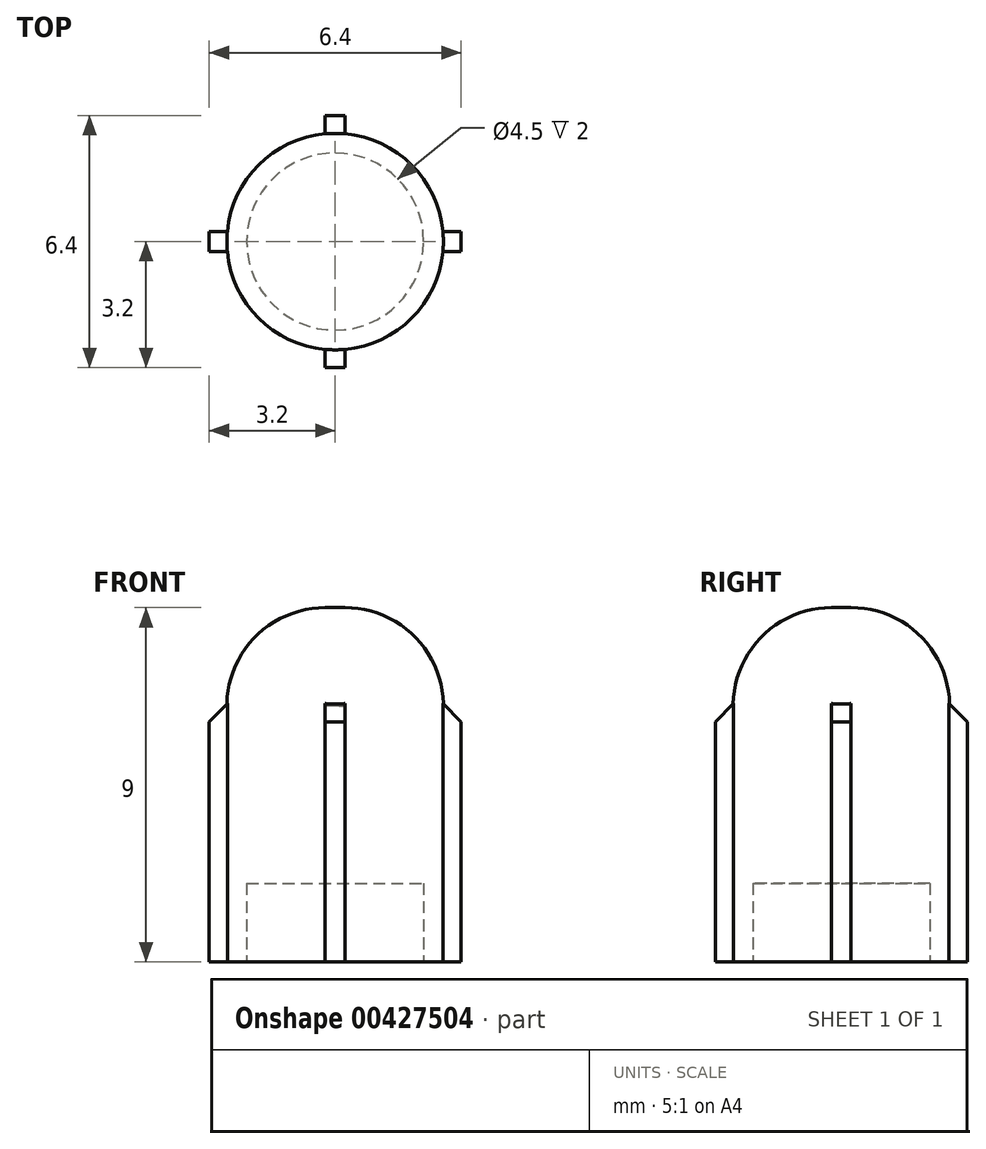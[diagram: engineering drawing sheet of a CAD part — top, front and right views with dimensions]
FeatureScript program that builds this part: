
annotation { "Feature Type Name" : "Feature", "Feature Type Description" : "" }
export const myFeature = defineFeature(function(context is Context, id is Id, definition is map)
    precondition{}
    {
        {
            var Q0;
            Q0=qCreatedBy(makeId("Top.planeOp"),FACE);
            var sketch = newSketch(context, id + "F0", { "sketchPlane" : qUnion([Q0])});
            skCircle(sketch, "E0", {"center": v(0, 0) * mm, "radius": 2.75 * mm});
            skSolve(sketch);
        }
        {
            var Q0;
            Q0 = qSketchRegion(id + "F0", true);
            extrude(context, id + "F1", {"entities" : qUnion([Q0]), "depth" : 9 * mm});
        }
        {
            var Q0;
            Q0=makeQuery(id+"F1.opExtrude","CAP_FACE",FACE,{"disambiguationData":[OSD([sQuery(id+"F0.wireOp",EDGE,"E0")])],"isStart":false});
            fillet(context, id + "F2", {"entities" : qUnion([Q0]), "radius" : 2.5 * mm, "tangentPropagation" : true, "allowEdgeOverflow" : false});
        }
        {
            var Q0;
            Q0=makeQuery(id+"F1.opExtrude","CAP_FACE",FACE,{"disambiguationData":[OSD([sQuery(id+"F0.wireOp",EDGE,"E0")])],"isStart":true});
            var sketch = newSketch(context, id + "F3", { "sketchPlane" : qUnion([Q0])});
            skLineSegment(sketch, "E1.bottom", {"start": v(-3.2, 0.25) * mm, "end": v(3.2, 0.25) * mm});
            skLineSegment(sketch, "E1.top", {"start": v(-3.2, -0.25) * mm, "end": v(3.2, -0.25) * mm});
            skLineSegment(sketch, "E1.left", {"start": v(-3.2, 0.25) * mm, "end": v(-3.2, -0.25) * mm});
            skLineSegment(sketch, "E1.right", {"start": v(3.2, 0.25) * mm, "end": v(3.2, -0.25) * mm});
            skSolve(sketch);
        }
        {
            var Q0;
            Q0 = qSketchRegion(id + "F3", true);
            extrude(context, id + "F4", {"entities" : qUnion([Q0]), "operationType" : NewBodyOperationType.ADD, "oppositeDirection" : true, "depth" : 7.5 * mm});
        }
        {
            var Q0;
            Q0=makeQuery(id+"F4.boolean.opBoolean","MERGE",FACE,{"derivedFrom":[makeQuery(id+"F1.opExtrude","CAP_FACE",FACE,{"disambiguationData":[OSD([sQuery(id+"F0.wireOp",EDGE,"E0")])],"isStart":true}),makeQuery(id+"F4.opExtrude","CAP_FACE",FACE,{"disambiguationData":[OSD([sQuery(id+"F3.wireOp",EDGE,"E1.bottom"),sQuery(id+"F3.wireOp",EDGE,"E1.top"),sQuery(id+"F3.wireOp",EDGE,"E1.left"),sQuery(id+"F3.wireOp",EDGE,"E1.right")])],"isStart":true})]});
            var sketch = newSketch(context, id + "F5", { "sketchPlane" : qUnion([Q0])});
            skLineSegment(sketch, "E2.bottom", {"start": v(-0.25, 3.2) * mm, "end": v(0.25, 3.2) * mm});
            skLineSegment(sketch, "E2.top", {"start": v(-0.25, -3.2) * mm, "end": v(0.25, -3.2) * mm});
            skLineSegment(sketch, "E2.left", {"start": v(-0.25, 3.2) * mm, "end": v(-0.25, 2.74) * mm});
            skLineSegment(sketch, "E2.right", {"start": v(0.25, 3.2) * mm, "end": v(0.25, 2.74) * mm});
            skPoint(sketch, "E3", {"position": v(0.25, 2.74) * mm});
            skPoint(sketch, "E4", {"position": v(-0.25, 2.74) * mm});
            skPoint(sketch, "E5", {"position": v(0.25, -2.74) * mm});
            skPoint(sketch, "E6", {"position": v(-0.25, -2.74) * mm});
            skLineSegment(sketch, "E7.trimOffspring", {"start": v(0.25, -2.74) * mm, "end": v(0.25, -3.2) * mm});
            skLineSegment(sketch, "E8.trimOffspring", {"start": v(-0.25, -2.74) * mm, "end": v(-0.25, -3.2) * mm});
            skFitSpline(sketch, "E9", {"points": [v(-0.25, 2.74) * mm, v(-0.11, 2.75) * mm, v(0.1, 2.75) * mm, v(0.25, 2.74) * mm], "startDerivative": vector(0.45, 0.03) * mm, "endDerivative": vector(0.47, -0.03) * mm});
            skSolve(sketch);
        }
        {
            var Q0;
            Q0=makeQuery(id+"F4.opExtrude","CAP_EDGE",EDGE,{"disambiguationData":[OSD([sQuery(id+"F3.wireOp",EDGE,"E1.left")])],"isStart":false});
            var Q1;
            Q1=makeQuery(id+"F4.opExtrude","CAP_EDGE",EDGE,{"disambiguationData":[OSD([sQuery(id+"F3.wireOp",EDGE,"E1.right")])],"isStart":false});
            chamfer(context, id + "F6", {"entities" : qUnion([Q0, Q1]), "width" : 1.4 * mm, "tangentPropagation" : true});
        }
        {
            var Q0;
            Q0=makeQuery(id+"F5.imprint","IMPRINT",FACE,{"disambiguationData":[TD([[makeQuery(id+"F5.imprint","IMPRINT",EDGE,{"derivedFrom":sQuery(id+"F5.wireOp",EDGE,"E2.bottom")}),-1.0]])]});
            var Q1;
            Q1=makeQuery(id+"F5.imprint","IMPRINT",FACE,{"disambiguationData":[TD([[makeQuery(id+"F5.imprint","IMPRINT",EDGE,{"derivedFrom":sQuery(id+"F5.wireOp",EDGE,"E2.top")}),1.0]])]});
            extrude(context, id + "F7", {"entities" : qUnion([Q0, Q1]), "operationType" : NewBodyOperationType.ADD, "oppositeDirection" : true, "depth" : 7.5 * mm});
        }
        {
            var Q0;
            Q0=makeQuery(id+"F7.opExtrude","CAP_EDGE",EDGE,{"disambiguationData":[OSD([sQuery(id+"F5.wireOp",EDGE,"E2.top")])],"isStart":false});
            var Q1;
            Q1=makeQuery(id+"F7.opExtrude","CAP_EDGE",EDGE,{"disambiguationData":[OSD([sQuery(id+"F5.wireOp",EDGE,"E2.bottom")])],"isStart":false});
            chamfer(context, id + "F8", {"entities" : qUnion([Q0, Q1]), "width" : 1.4 * mm, "tangentPropagation" : true});
        }
        {
            var Q0;
            {var subQ0=sQuery(id+"F0.wireOp",EDGE,"E0");Q0=makeQuery(id+"F7.boolean.opBoolean","MERGE",FACE,{"derivedFrom":[makeQuery(id+"F4.boolean.opBoolean","MERGE",FACE,{"derivedFrom":[makeQuery(id+"F1.opExtrude","CAP_FACE",FACE,{"disambiguationData":[OSD([subQ0])],"isStart":true}),makeQuery(id+"F4.opExtrude","CAP_FACE",FACE,{"disambiguationData":[OSD([sQuery(id+"F3.wireOp",EDGE,"E1.bottom"),sQuery(id+"F3.wireOp",EDGE,"E1.top"),sQuery(id+"F3.wireOp",EDGE,"E1.left"),sQuery(id+"F3.wireOp",EDGE,"E1.right")])],"isStart":true})]}),makeQuery(id+"F7.opExtrude","CAP_FACE",FACE,{"disambiguationData":[OSD([subQ0,sQuery(id+"F5.wireOp",EDGE,"E2.bottom"),sQuery(id+"F5.wireOp",EDGE,"E2.left"),sQuery(id+"F5.wireOp",EDGE,"E2.right"),sQuery(id+"F5.wireOp",EDGE,"E9")])],"isStart":true}),makeQuery(id+"F7.opExtrude","CAP_FACE",FACE,{"disambiguationData":[OSD([subQ0,sQuery(id+"F5.wireOp",EDGE,"E2.top"),sQuery(id+"F5.wireOp",EDGE,"E7.trimOffspring"),sQuery(id+"F5.wireOp",EDGE,"E8.trimOffspring")])],"isStart":true})]});}
            var sketch = newSketch(context, id + "F9", { "sketchPlane" : qUnion([Q0])});
            skCircle(sketch, "E10", {"center": v(0, 0) * mm, "radius": 2.25 * mm});
            skSolve(sketch);
        }
        {
            var Q0;
            Q0 = qSketchRegion(id + "F9", true);
            extrude(context, id + "F10", {"entities" : qUnion([Q0]), "operationType" : NewBodyOperationType.REMOVE, "oppositeDirection" : true, "depth" : 2 * mm});
        }
    });
